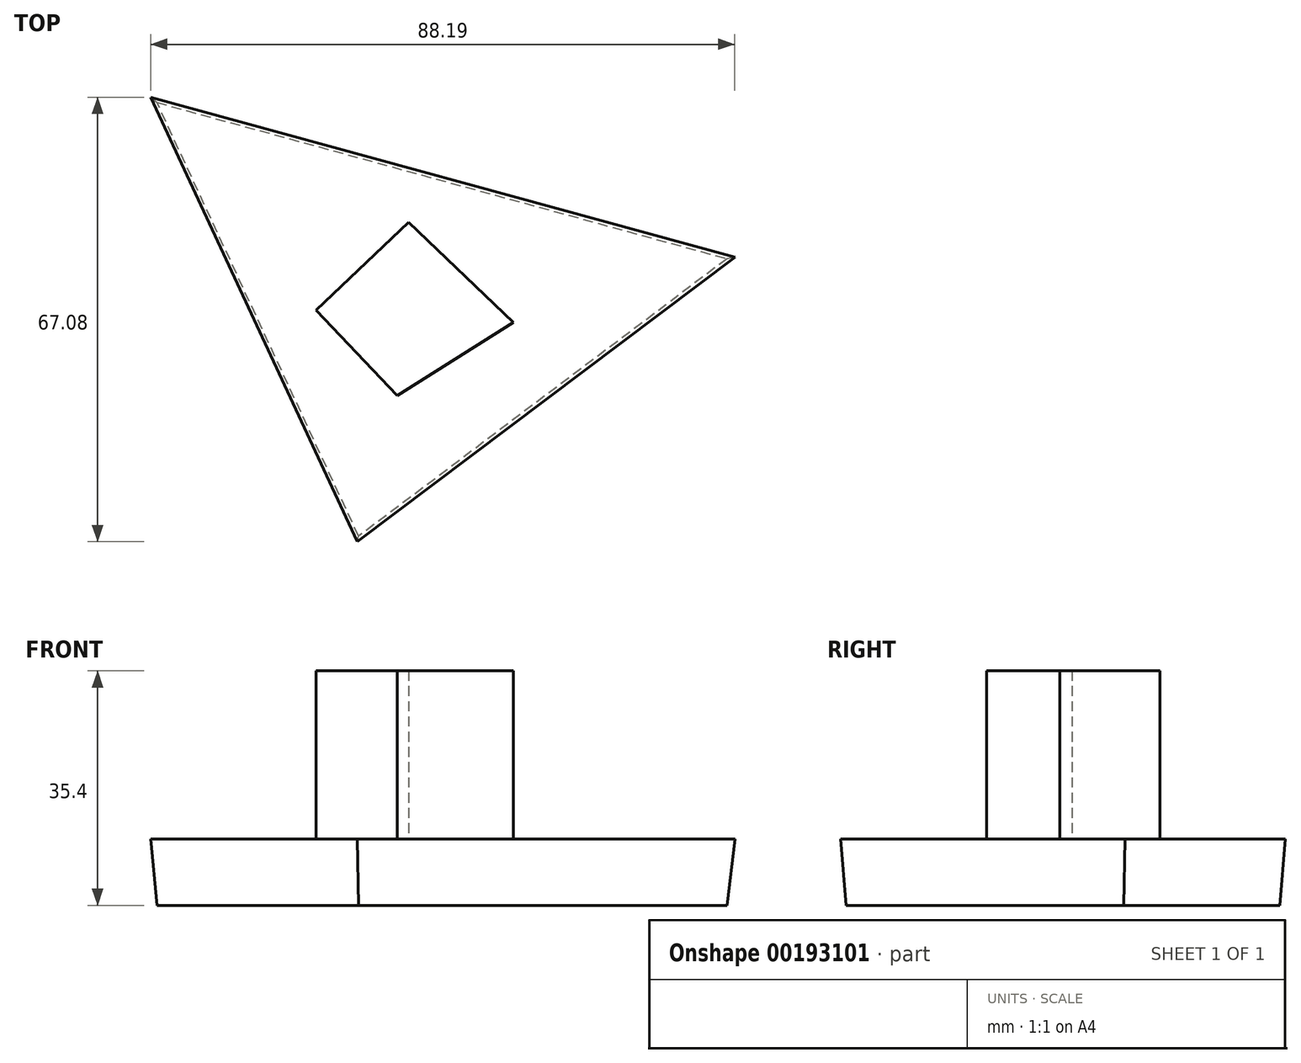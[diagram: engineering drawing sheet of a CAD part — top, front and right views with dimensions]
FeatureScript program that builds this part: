
annotation { "Feature Type Name" : "Feature", "Feature Type Description" : "" }
export const myFeature = defineFeature(function(context is Context, id is Id, definition is map)
    precondition{}
    {
        {
            var Q0;
            Q0=qCreatedBy(makeId("Top.planeOp"),FACE);
            var sketch = newSketch(context, id + "F0", { "sketchPlane" : qUnion([Q0])});
            skLineSegment(sketch, "E0", {"start": v(-38, 35.14) * mm, "end": v(48.07, 11.56) * mm});
            skLineSegment(sketch, "E1", {"start": v(48.07, 11.56) * mm, "end": v(-7.55, -30.33) * mm});
            skLineSegment(sketch, "E2", {"start": v(-7.55, -30.33) * mm, "end": v(-38, 35.14) * mm});
            skSolve(sketch);
        }
        {
            var Q0;
            Q0 = qSketchRegion(id + "F0", true);
            extrude(context, id + "F1", {"entities" : qUnion([Q0]), "depth" : 10 * mm, "hasDraft" : true, "draftAngle" : 3 * degree});
        }
        {
            var Q0;
            Q0=makeQuery(id+"F1.opExtrude","CAP_FACE",FACE,{"disambiguationData":[OSD([sQuery(id+"F0.wireOp",EDGE,"E0"),sQuery(id+"F0.wireOp",EDGE,"E1"),sQuery(id+"F0.wireOp",EDGE,"E2")])],"isStart":false});
            var sketch = newSketch(context, id + "F2", { "sketchPlane" : qUnion([Q0])});
            skLineSegment(sketch, "E3", {"start": v(0, 17.06) * mm, "end": v(-13.96, 3.78) * mm});
            skLineSegment(sketch, "E4", {"start": v(-13.96, 3.78) * mm, "end": v(-1.7, -9.12) * mm});
            skLineSegment(sketch, "E5", {"start": v(-1.7, -9.12) * mm, "end": v(15.8, 1.95) * mm});
            skLineSegment(sketch, "E6", {"start": v(15.8, 1.95) * mm, "end": v(0, 17.06) * mm});
            skSolve(sketch);
        }
        {
            var Q0;
            Q0 = qSketchRegion(id + "F2", true);
            extrude(context, id + "F3", {"entities" : qUnion([Q0]), "operationType" : NewBodyOperationType.ADD, "depth" : 25.4 * mm});
        }
    });
